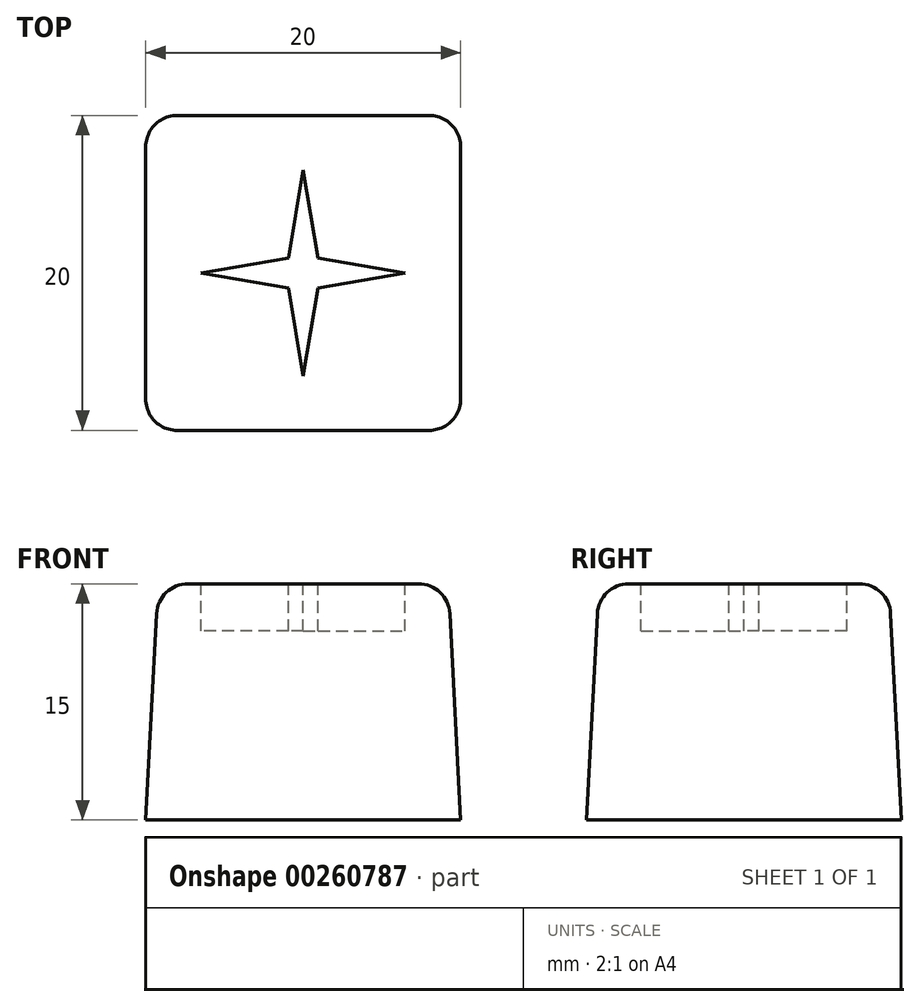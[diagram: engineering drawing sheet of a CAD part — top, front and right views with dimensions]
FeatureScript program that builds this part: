
annotation { "Feature Type Name" : "Feature", "Feature Type Description" : "" }
export const myFeature = defineFeature(function(context is Context, id is Id, definition is map)
    precondition{}
    {
        {
            var Q0;
            Q0=qCreatedBy(makeId("Top.planeOp"),FACE);
            var sketch = newSketch(context, id + "F0", { "sketchPlane" : qUnion([Q0])});
            skLineSegment(sketch, "E0.bottom", {"start": v(-8.13, 6.89) * mm, "end": v(11.87, 6.89) * mm});
            skLineSegment(sketch, "E0.top", {"start": v(-8.13, -13.11) * mm, "end": v(11.87, -13.11) * mm});
            skLineSegment(sketch, "E0.left", {"start": v(-8.13, 6.89) * mm, "end": v(-8.13, -13.11) * mm});
            skLineSegment(sketch, "E0.right", {"start": v(11.87, 6.89) * mm, "end": v(11.87, -13.11) * mm});
            skSolve(sketch);
        }
        {
            var Q0;
            Q0 = qSketchRegion(id + "F0", true);
            extrude(context, id + "F1", {"entities" : qUnion([Q0]), "depth" : 15 * mm, "hasDraft" : true, "draftAngle" : 3 * degree, "draftPullDirection" : true});
        }
        {
            var Q0;
            Q0=makeQuery(id+"F1.opExtrude","SWEPT_EDGE",EDGE,{"disambiguationData":[OSD([sQuery(id+"F0.wireOp",EDGE,"E0.bottom"),sQuery(id+"F0.wireOp",EDGE,"E0.left")])]});
            var Q1;
            Q1=makeQuery(id+"F1.opExtrude","CAP_EDGE",EDGE,{"disambiguationData":[OSD([sQuery(id+"F0.wireOp",EDGE,"E0.bottom")])],"isStart":false});
            var Q2;
            Q2=makeQuery(id+"F1.opExtrude","SWEPT_EDGE",EDGE,{"disambiguationData":[OSD([sQuery(id+"F0.wireOp",EDGE,"E0.bottom"),sQuery(id+"F0.wireOp",EDGE,"E0.right")])]});
            var Q3;
            Q3=makeQuery(id+"F1.opExtrude","CAP_EDGE",EDGE,{"disambiguationData":[OSD([sQuery(id+"F0.wireOp",EDGE,"E0.right")])],"isStart":false});
            var Q4;
            Q4=makeQuery(id+"F1.opExtrude","SWEPT_EDGE",EDGE,{"disambiguationData":[OSD([sQuery(id+"F0.wireOp",EDGE,"E0.top"),sQuery(id+"F0.wireOp",EDGE,"E0.right")])]});
            var Q5;
            Q5=makeQuery(id+"F1.opExtrude","CAP_EDGE",EDGE,{"disambiguationData":[OSD([sQuery(id+"F0.wireOp",EDGE,"E0.top")])],"isStart":false});
            var Q6;
            Q6=makeQuery(id+"F1.opExtrude","CAP_EDGE",EDGE,{"disambiguationData":[OSD([sQuery(id+"F0.wireOp",EDGE,"E0.left")])],"isStart":false});
            var Q7;
            Q7=makeQuery(id+"F1.opExtrude","SWEPT_EDGE",EDGE,{"disambiguationData":[OSD([sQuery(id+"F0.wireOp",EDGE,"E0.top"),sQuery(id+"F0.wireOp",EDGE,"E0.left")])]});
            fillet(context, id + "F2", {"entities" : qUnion([Q0, Q1, Q2, Q3, Q4, Q5, Q6, Q7]), "radius" : 2 * mm, "tangentPropagation" : true, "allowEdgeOverflow" : false});
        }
        {
            var Q0;
            Q0=makeQuery(id+"F1.opExtrude","CAP_FACE",FACE,{"disambiguationData":[OSD([sQuery(id+"F0.wireOp",EDGE,"E0.bottom"),sQuery(id+"F0.wireOp",EDGE,"E0.top"),sQuery(id+"F0.wireOp",EDGE,"E0.left"),sQuery(id+"F0.wireOp",EDGE,"E0.right")])],"isStart":false});
            var sketch = newSketch(context, id + "F3", { "sketchPlane" : qUnion([Q0])});
            skLineSegment(sketch, "E1", {"start": v(1.87, 3.43) * mm, "end": v(0.93, -2.15) * mm});
            skLineSegment(sketch, "E2", {"start": v(0.93, -2.15) * mm, "end": v(-4.6, -3.11) * mm});
            skLineSegment(sketch, "E3.MirrorCS", {"start": v(1.87, 3.43) * mm, "end": v(2.81, -2.15) * mm});
            skLineSegment(sketch, "E4.MirrorCS", {"start": v(2.81, -2.15) * mm, "end": v(8.34, -3.11) * mm});
            skLineSegment(sketch, "E5.MirrorCS", {"start": v(2.81, -4.07) * mm, "end": v(8.34, -3.11) * mm});
            skLineSegment(sketch, "E6.MirrorCS", {"start": v(1.87, -9.65) * mm, "end": v(2.81, -4.07) * mm});
            skLineSegment(sketch, "E7.MirrorCS", {"start": v(1.87, -9.65) * mm, "end": v(0.93, -4.07) * mm});
            skLineSegment(sketch, "E8.MirrorCS", {"start": v(0.93, -4.07) * mm, "end": v(-4.6, -3.11) * mm});
            skPoint(sketch, "E9.start.orphan", {"position": v(1.87, 4.2) * mm});
            skPoint(sketch, "E10.orphan", {"position": v(9.19, -3.11) * mm});
            skPoint(sketch, "E11.start.orphan", {"position": v(-5.45, -3.11) * mm});
            skPoint(sketch, "E12.trimOffspring.end.orphan", {"position": v(1.87, -10.43) * mm});
            skSolve(sketch);
        }
        {
            var Q0;
            Q0 = qSketchRegion(id + "F3", true);
            extrude(context, id + "F4", {"entities" : qUnion([Q0]), "operationType" : NewBodyOperationType.REMOVE, "oppositeDirection" : true, "depth" : 3 * mm});
        }
    });
